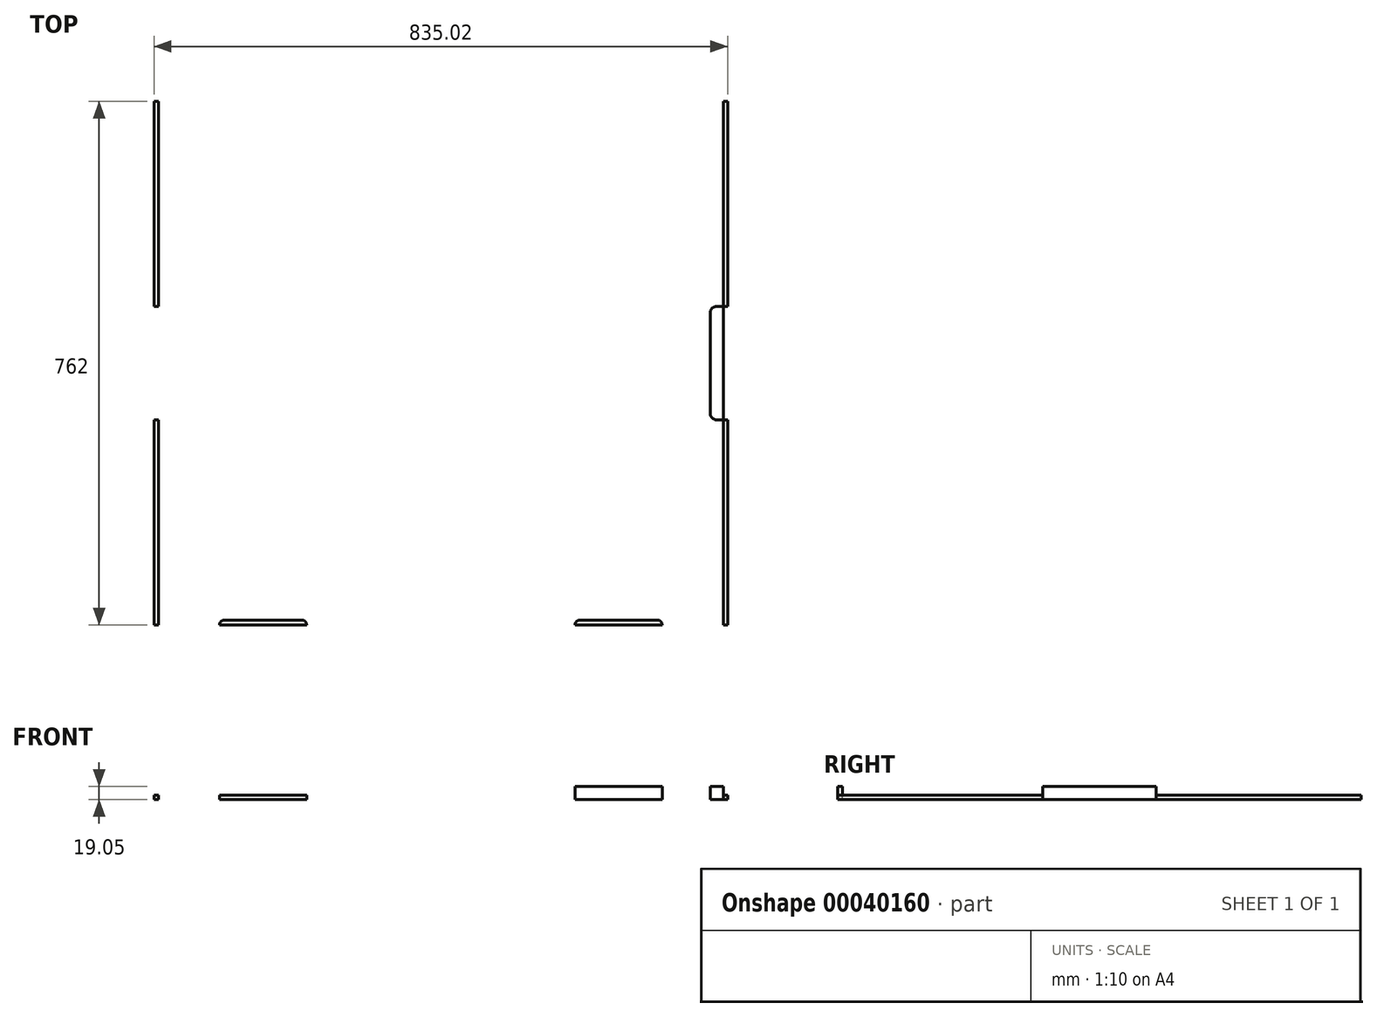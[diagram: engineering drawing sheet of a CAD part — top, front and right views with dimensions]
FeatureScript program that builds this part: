
annotation { "Feature Type Name" : "Feature", "Feature Type Description" : "" }
export const myFeature = defineFeature(function(context is Context, id is Id, definition is map)
    precondition{}
    {
        {
            var Q0;
            Q0=qCreatedBy(makeId("Top.planeOp"),FACE);
            var sketch = newSketch(context, id + "F0", { "sketchPlane" : qUnion([Q0])});
            skLineSegment(sketch, "E0.rect.bottom", {"start": v(417.51, -381) * mm, "end": v(-417.51, -381) * mm});
            skLineSegment(sketch, "E0.rect.top", {"start": v(417.51, 381) * mm, "end": v(-417.51, 381) * mm});
            skLineSegment(sketch, "E0.rect.left", {"start": v(417.51, -381) * mm, "end": v(417.51, 381) * mm});
            skLineSegment(sketch, "E0.rect.right", {"start": v(-417.51, -381) * mm, "end": v(-417.51, 381) * mm});
            skPoint(sketch, "E0.rect.middle", {"position": v(0, 0) * mm});
            skSolve(sketch);
        }
        {
            var Q0;
            Q0=makeQuery(id+"F0.imprint","IMPRINT",FACE,{"disambiguationData":[TD([[makeQuery(id+"F0.imprint","IMPRINT",EDGE,{"derivedFrom":sQuery(id+"F0.wireOp",EDGE,"E0.rect.bottom")}),-1.0]])]});
            extrude(context, id + "F1", {"entities" : qUnion([Q0]), "depth" : 19.05 * mm});
        }
        {
            var Q0;
            Q0=makeQuery(id+"F1.opExtrude","CAP_FACE",FACE,{"disambiguationData":[OSD([sQuery(id+"F0.wireOp",EDGE,"E0.rect.bottom"),sQuery(id+"F0.wireOp",EDGE,"E0.rect.top"),sQuery(id+"F0.wireOp",EDGE,"E0.rect.left"),sQuery(id+"F0.wireOp",EDGE,"E0.rect.right")])],"isStart":false});
            var sketch = newSketch(context, id + "F2", { "sketchPlane" : qUnion([Q0])});
            skLineSegment(sketch, "E1.bottom", {"start": v(-423.86, 82.55) * mm, "end": v(-401.64, 82.55) * mm});
            skLineSegment(sketch, "E1.top", {"start": v(-423.86, -82.55) * mm, "end": v(-401.64, -82.55) * mm});
            skLineSegment(sketch, "E1.left", {"start": v(-423.86, 82.55) * mm, "end": v(-423.86, -82.55) * mm});
            skLineSegment(sketch, "E1.right", {"start": v(-392.11, 73.02) * mm, "end": v(-392.11, -73.03) * mm});
            skLineSegment(sketch, "E2.bottom", {"start": v(-195.26, -386.56) * mm, "end": v(-322.26, -386.56) * mm});
            skLineSegment(sketch, "E2.top", {"start": v(-202.4, -373.86) * mm, "end": v(-315.12, -373.86) * mm});
            skLineSegment(sketch, "E2.left", {"start": v(-195.26, -386.56) * mm, "end": v(-195.26, -381) * mm});
            skLineSegment(sketch, "E2.right", {"start": v(-322.26, -386.56) * mm, "end": v(-322.26, -381) * mm});
            skLineSegment(sketch, "E3.bottom", {"start": v(-461.96, 387.35) * mm, "end": v(-411.16, 387.35) * mm});
            skLineSegment(sketch, "E3.top", {"start": v(-461.96, -387.35) * mm, "end": v(-411.16, -387.35) * mm});
            skLineSegment(sketch, "E3.left", {"start": v(-461.96, 387.35) * mm, "end": v(-461.96, -387.35) * mm});
            skLineSegment(sketch, "E3.right", {"start": v(-411.16, 387.35) * mm, "end": v(-411.16, -387.35) * mm});
            skPoint(sketch, "E4.visualSharp", {"position": v(-392.11, 82.55) * mm});
            skArc(sketch, "E4.filletArc", {"start": v(-392.11, 73.02) * mm, "mid": v(-394.9, 79.76) * mm, "end": v(-401.64, 82.55) * mm});
            skPoint(sketch, "E5.visualSharp", {"position": v(-392.11, -82.55) * mm});
            skArc(sketch, "E5.filletArc", {"start": v(-401.64, -82.55) * mm, "mid": v(-394.9, -79.76) * mm, "end": v(-392.11, -73.03) * mm});
            skLineSegment(sketch, "E6", {"start": v(0, 0) * mm, "end": v(0, 252.74) * mm, "construction": true});
            skArc(sketch, "E7.MirrorCS", {"start": v(392.11, 73.02) * mm, "mid": v(394.9, 79.76) * mm, "end": v(401.64, 82.55) * mm});
            skArc(sketch, "E8.MirrorCS", {"start": v(401.64, -82.55) * mm, "mid": v(394.9, -79.76) * mm, "end": v(392.11, -73.03) * mm});
            skLineSegment(sketch, "E9.MirrorCS", {"start": v(392.11, 73.02) * mm, "end": v(392.11, -73.03) * mm});
            skLineSegment(sketch, "E10.MirrorCS", {"start": v(461.96, 387.35) * mm, "end": v(411.16, 387.35) * mm});
            skLineSegment(sketch, "E11.MirrorCS", {"start": v(461.96, -387.35) * mm, "end": v(411.16, -387.35) * mm});
            skLineSegment(sketch, "E12.MirrorCS", {"start": v(461.96, 387.35) * mm, "end": v(461.96, -387.35) * mm});
            skLineSegment(sketch, "E13.MirrorCS", {"start": v(411.16, 387.35) * mm, "end": v(411.16, -387.35) * mm});
            skLineSegment(sketch, "E14.MirrorCS", {"start": v(423.86, 82.55) * mm, "end": v(423.86, -82.55) * mm});
            skLineSegment(sketch, "E15.MirrorCS", {"start": v(423.86, -82.55) * mm, "end": v(401.64, -82.55) * mm});
            skLineSegment(sketch, "E16.MirrorCS", {"start": v(423.86, 82.55) * mm, "end": v(401.64, 82.55) * mm});
            skPoint(sketch, "E17.MirrorP", {"position": v(392.11, -82.55) * mm});
            skPoint(sketch, "E18.MirrorP", {"position": v(392.11, 82.55) * mm});
            skPoint(sketch, "E19.visualSharp", {"position": v(-322.26, -373.86) * mm});
            skArc(sketch, "E19.filletArc", {"start": v(-315.12, -373.86) * mm, "mid": v(-320.17, -375.95) * mm, "end": v(-322.26, -381) * mm});
            skPoint(sketch, "E20.visualSharp", {"position": v(-195.26, -373.86) * mm});
            skArc(sketch, "E20.filletArc", {"start": v(-195.26, -381) * mm, "mid": v(-197.35, -375.95) * mm, "end": v(-202.4, -373.86) * mm});
            skLineSegment(sketch, "E21.MirrorCS", {"start": v(195.26, -386.56) * mm, "end": v(195.26, -381) * mm});
            skLineSegment(sketch, "E22.MirrorCS", {"start": v(322.26, -386.56) * mm, "end": v(322.26, -381) * mm});
            skArc(sketch, "E23.MirrorCS", {"start": v(195.26, -381) * mm, "mid": v(197.35, -375.95) * mm, "end": v(202.4, -373.86) * mm});
            skArc(sketch, "E24.MirrorCS", {"start": v(315.12, -373.86) * mm, "mid": v(320.17, -375.95) * mm, "end": v(322.26, -381) * mm});
            skPoint(sketch, "E25.MirrorP", {"position": v(322.26, -373.86) * mm});
            skPoint(sketch, "E26.MirrorP", {"position": v(195.26, -373.86) * mm});
            skLineSegment(sketch, "E27.MirrorCS", {"start": v(202.4, -373.86) * mm, "end": v(315.12, -373.86) * mm});
            skLineSegment(sketch, "E28.MirrorCS", {"start": v(195.26, -386.56) * mm, "end": v(322.26, -386.56) * mm});
            skSolve(sketch);
        }
        {
            var Q0;
            {var subQ5=sQuery(id+"F2.wireOp",EDGE,"E1.left");Q0=makeQuery(id+"F2.imprint","IMPRINT",FACE,{"disambiguationData":[TD([[makeQuery(id+"F2.imprint","IMPRINT",EDGE,{"derivedFrom":subQ5}),1.0]])]});}
            var Q1;
            {var subQ3=sQuery(id+"F2.wireOp",EDGE,"E1.bottom");var subQ5=sQuery(id+"F2.wireOp",EDGE,"E3.right");var subQ7=makeQuery(id+"F2.imprint","INTERSECT",VERTEX,{"derivedFrom":[subQ3,subQ5]});Q1=makeQuery(id+"F2.imprint","IMPRINT",FACE,{"disambiguationData":[TD([[makeQuery(id+"F2.imprint","IMPRINT",EDGE,{"disambiguationData":[TD([[subQ7,1.0]])],"derivedFrom":subQ3}),-1.0]])]});}
            var Q2;
            Q2=makeQuery(id+"F2.imprint","IMPRINT",FACE,{"disambiguationData":[TD([[makeQuery(id+"F2.imprint","IMPRINT",EDGE,{"derivedFrom":sQuery(id+"F2.wireOp",EDGE,"E1.right")}),-1.0]])]});
            var Q3;
            {var subQ0=sQuery(id+"F2.wireOp",EDGE,"E7.MirrorCS");Q3=makeQuery(id+"F2.imprint","IMPRINT",FACE,{"disambiguationData":[TD([[makeQuery(id+"F2.imprint","IMPRINT",EDGE,{"derivedFrom":subQ0}),-1.0]])]});}
            var Q4;
            {var subQ5=sQuery(id+"F2.wireOp",EDGE,"E14.MirrorCS");Q4=makeQuery(id+"F2.imprint","IMPRINT",FACE,{"disambiguationData":[TD([[makeQuery(id+"F2.imprint","IMPRINT",EDGE,{"derivedFrom":subQ5}),-1.0]])]});}
            var Q5;
            {var subQ0=sQuery(id+"F2.wireOp",EDGE,"E16.MirrorCS");var subQ3=sQuery(id+"F2.wireOp",EDGE,"E13.MirrorCS");var subQ4=makeQuery(id+"F2.imprint","INTERSECT",VERTEX,{"derivedFrom":[subQ3,subQ0]});Q5=makeQuery(id+"F2.imprint","IMPRINT",FACE,{"disambiguationData":[TD([[makeQuery(id+"F2.imprint","IMPRINT",EDGE,{"disambiguationData":[TD([[subQ4,-1.0]])],"derivedFrom":subQ3}),1.0]])]});}
            extrude(context, id + "F3", {"entities" : qUnion([Q0, Q1, Q2, Q3, Q4, Q5]), "operationType" : NewBodyOperationType.REMOVE, "endBound" : BoundingType.THROUGH_ALL, "oppositeDirection" : true, "depth" : 25.4 * mm});
        }
        {
            var Q0;
            {var subQ1=sQuery(id+"F2.wireOp",EDGE,"E1.bottom");var subQ5=sQuery(id+"F2.wireOp",EDGE,"E3.right");var subQ7=makeQuery(id+"F2.imprint","INTERSECT",VERTEX,{"derivedFrom":[subQ1,subQ5]});Q0=makeQuery(id+"F2.imprint","IMPRINT",FACE,{"disambiguationData":[TD([[makeQuery(id+"F2.imprint","IMPRINT",EDGE,{"disambiguationData":[TD([[subQ7,1.0]])],"derivedFrom":subQ1}),1.0]])]});}
            var Q1;
            {var subQ1=sQuery(id+"F2.wireOp",EDGE,"E1.top");var subQ5=sQuery(id+"F2.wireOp",EDGE,"E3.right");var subQ7=makeQuery(id+"F2.imprint","INTERSECT",VERTEX,{"derivedFrom":[subQ1,subQ5]});Q1=makeQuery(id+"F2.imprint","IMPRINT",FACE,{"disambiguationData":[TD([[makeQuery(id+"F2.imprint","IMPRINT",EDGE,{"disambiguationData":[TD([[subQ7,1.0]])],"derivedFrom":subQ1}),-1.0]])]});}
            var Q2;
            {var subQ1=sQuery(id+"F2.wireOp",EDGE,"E13.MirrorCS");var subQ5=sQuery(id+"F2.wireOp",EDGE,"E16.MirrorCS");var subQ7=makeQuery(id+"F2.imprint","INTERSECT",VERTEX,{"derivedFrom":[subQ1,subQ5]});Q2=makeQuery(id+"F2.imprint","IMPRINT",FACE,{"disambiguationData":[TD([[makeQuery(id+"F2.imprint","IMPRINT",EDGE,{"disambiguationData":[TD([[subQ7,1.0]])],"derivedFrom":subQ1}),1.0]])]});}
            var Q3;
            {var subQ1=sQuery(id+"F2.wireOp",EDGE,"E13.MirrorCS");var subQ5=sQuery(id+"F2.wireOp",EDGE,"E15.MirrorCS");var subQ7=makeQuery(id+"F2.imprint","INTERSECT",VERTEX,{"derivedFrom":[subQ1,subQ5]});Q3=makeQuery(id+"F2.imprint","IMPRINT",FACE,{"disambiguationData":[TD([[makeQuery(id+"F2.imprint","IMPRINT",EDGE,{"disambiguationData":[TD([[subQ7,-1.0]])],"derivedFrom":subQ1}),1.0]])]});}
            var Q4;
            {var subQ2=sQuery(id+"F2.wireOp",EDGE,"E23.MirrorCS");Q4=makeQuery(id+"F2.imprint","IMPRINT",FACE,{"disambiguationData":[TD([[makeQuery(id+"F2.imprint","IMPRINT",EDGE,{"derivedFrom":subQ2}),-1.0]])]});}
            var Q5;
            Q5=makeQuery(id+"F2.imprint","IMPRINT",FACE,{"disambiguationData":[TD([[makeQuery(id+"F2.imprint","IMPRINT",EDGE,{"derivedFrom":sQuery(id+"F2.wireOp",EDGE,"E2.top")}),1.0]])]});
            extrude(context, id + "F4", {"entities" : qUnion([Q0, Q1, Q2, Q3, Q4, Q5]), "operationType" : NewBodyOperationType.REMOVE, "oppositeDirection" : true, "depth" : 12.7 * mm});
        }
        {
            var Q0;
            Q0=makeQuery(id+"F1.opExtrude","CAP_FACE",FACE,{"disambiguationData":[OSD([sQuery(id+"F0.wireOp",EDGE,"E0.rect.bottom"),sQuery(id+"F0.wireOp",EDGE,"E0.rect.top"),sQuery(id+"F0.wireOp",EDGE,"E0.rect.left"),sQuery(id+"F0.wireOp",EDGE,"E0.rect.right")])],"isStart":false});
            var sketch = newSketch(context, id + "F5", { "sketchPlane" : qUnion([Q0])});
            skCircle(sketch, "E29", {"center": v(-368.3, 63.5) * mm, "radius": 4.01 * mm});
            skLineSegment(sketch, "E30", {"start": v(0, 0) * mm, "end": v(0, 204.5) * mm, "construction": true});
            skLineSegment(sketch, "E31", {"start": v(0, 0) * mm, "end": v(-237.68, 0) * mm, "construction": true});
            skCircle(sketch, "E32.0.1.0", {"center": v(-368.3, 88.9) * mm, "radius": 4.01 * mm});
            skCircle(sketch, "E32.0.2.0", {"center": v(-368.3, 114.3) * mm, "radius": 4.01 * mm});
            skCircle(sketch, "E32.0.3.0", {"center": v(-368.3, 139.7) * mm, "radius": 4.01 * mm});
            skCircle(sketch, "E32.0.4.0", {"center": v(-368.3, 165.1) * mm, "radius": 4.01 * mm});
            skCircle(sketch, "E32.0.5.0", {"center": v(-368.3, 190.5) * mm, "radius": 4.01 * mm});
            skCircle(sketch, "E32.0.6.0", {"center": v(-368.3, 215.9) * mm, "radius": 4.01 * mm});
            skCircle(sketch, "E32.0.7.0", {"center": v(-368.3, 241.3) * mm, "radius": 4.01 * mm});
            skCircle(sketch, "E32.0.8.0", {"center": v(-368.3, 266.7) * mm, "radius": 4.01 * mm});
            skCircle(sketch, "E32.0.9.0", {"center": v(-368.3, 292.1) * mm, "radius": 4.01 * mm});
            skCircle(sketch, "E32.0.10.0", {"center": v(-368.3, 317.5) * mm, "radius": 4.01 * mm});
            skCircle(sketch, "E32.0.11.0", {"center": v(-368.3, 342.9) * mm, "radius": 4.01 * mm});
            skCircle(sketch, "E32.0.12.0", {"center": v(-368.3, 368.3) * mm, "radius": 4.01 * mm});
            skLineSegment(sketch, "E32.direction1", {"start": v(-368.3, 63.5) * mm, "end": v(-342.9, 63.5) * mm, "construction": true});
            skLineSegment(sketch, "E32.direction2", {"start": v(-368.3, 63.5) * mm, "end": v(-368.3, 88.9) * mm, "construction": true});
            skCircle(sketch, "E33.MirrorC", {"center": v(368.3, 317.5) * mm, "radius": 4.01 * mm});
            skCircle(sketch, "E34.MirrorC", {"center": v(368.3, 292.1) * mm, "radius": 4.01 * mm});
            skCircle(sketch, "E35.MirrorC", {"center": v(368.3, 266.7) * mm, "radius": 4.01 * mm});
            skCircle(sketch, "E36.MirrorC", {"center": v(368.3, 241.3) * mm, "radius": 4.01 * mm});
            skCircle(sketch, "E37.MirrorC", {"center": v(368.3, 215.9) * mm, "radius": 4.01 * mm});
            skCircle(sketch, "E38.MirrorC", {"center": v(368.3, 190.5) * mm, "radius": 4.01 * mm});
            skCircle(sketch, "E39.MirrorC", {"center": v(368.3, 165.1) * mm, "radius": 4.01 * mm});
            skCircle(sketch, "E40.MirrorC", {"center": v(368.3, 139.7) * mm, "radius": 4.01 * mm});
            skCircle(sketch, "E41.MirrorC", {"center": v(368.3, 114.3) * mm, "radius": 4.01 * mm});
            skCircle(sketch, "E42.MirrorC", {"center": v(368.3, 368.3) * mm, "radius": 4.01 * mm});
            skCircle(sketch, "E43.MirrorC", {"center": v(368.3, 342.9) * mm, "radius": 4.01 * mm});
            skCircle(sketch, "E44.MirrorC", {"center": v(368.3, 88.9) * mm, "radius": 4.01 * mm});
            skCircle(sketch, "E45.MirrorC", {"center": v(368.3, 63.5) * mm, "radius": 4.01 * mm});
            skCircle(sketch, "E46.MirrorC", {"center": v(-368.3, -63.5) * mm, "radius": 4.01 * mm});
            skCircle(sketch, "E47.MirrorC", {"center": v(-368.3, -88.9) * mm, "radius": 4.01 * mm});
            skCircle(sketch, "E48.MirrorC", {"center": v(-368.3, -317.5) * mm, "radius": 4.01 * mm});
            skCircle(sketch, "E49.MirrorC", {"center": v(-368.3, -292.1) * mm, "radius": 4.01 * mm});
            skCircle(sketch, "E50.MirrorC", {"center": v(-368.3, -266.7) * mm, "radius": 4.01 * mm});
            skCircle(sketch, "E51.MirrorC", {"center": v(-368.3, -241.3) * mm, "radius": 4.01 * mm});
            skCircle(sketch, "E52.MirrorC", {"center": v(-368.3, -215.9) * mm, "radius": 4.01 * mm});
            skCircle(sketch, "E53.MirrorC", {"center": v(368.3, -292.1) * mm, "radius": 4.01 * mm});
            skCircle(sketch, "E54.MirrorC", {"center": v(-368.3, -190.5) * mm, "radius": 4.01 * mm});
            skCircle(sketch, "E55.MirrorC", {"center": v(-368.3, -165.1) * mm, "radius": 4.01 * mm});
            skCircle(sketch, "E56.MirrorC", {"center": v(-368.3, -139.7) * mm, "radius": 4.01 * mm});
            skCircle(sketch, "E57.MirrorC", {"center": v(368.3, -190.5) * mm, "radius": 4.01 * mm});
            skCircle(sketch, "E58.MirrorC", {"center": v(-368.3, -114.3) * mm, "radius": 4.01 * mm});
            skCircle(sketch, "E59.MirrorC", {"center": v(368.3, -368.3) * mm, "radius": 4.01 * mm});
            skCircle(sketch, "E60.MirrorC", {"center": v(368.3, -266.7) * mm, "radius": 4.01 * mm});
            skCircle(sketch, "E61.MirrorC", {"center": v(368.3, -342.9) * mm, "radius": 4.01 * mm});
            skCircle(sketch, "E62.MirrorC", {"center": v(368.3, -63.5) * mm, "radius": 4.01 * mm});
            skCircle(sketch, "E63.MirrorC", {"center": v(368.3, -241.3) * mm, "radius": 4.01 * mm});
            skCircle(sketch, "E64.MirrorC", {"center": v(368.3, -165.1) * mm, "radius": 4.01 * mm});
            skCircle(sketch, "E65.MirrorC", {"center": v(368.3, -317.5) * mm, "radius": 4.01 * mm});
            skCircle(sketch, "E66.MirrorC", {"center": v(368.3, -88.9) * mm, "radius": 4.01 * mm});
            skCircle(sketch, "E67.MirrorC", {"center": v(368.3, -139.7) * mm, "radius": 4.01 * mm});
            skCircle(sketch, "E68.MirrorC", {"center": v(368.3, -215.9) * mm, "radius": 4.01 * mm});
            skCircle(sketch, "E69.MirrorC", {"center": v(-368.3, -342.9) * mm, "radius": 4.01 * mm});
            skCircle(sketch, "E70.MirrorC", {"center": v(-368.3, -368.3) * mm, "radius": 4.01 * mm});
            skCircle(sketch, "E71.MirrorC", {"center": v(368.3, -114.3) * mm, "radius": 4.01 * mm});
            skLineSegment(sketch, "E72.MirrorCS", {"start": v(-368.3, -63.5) * mm, "end": v(-342.9, -63.5) * mm});
            skLineSegment(sketch, "E73.MirrorCS", {"start": v(-368.3, -63.5) * mm, "end": v(-368.3, -88.9) * mm});
            skCircle(sketch, "E74", {"center": v(-368.3, 0) * mm, "radius": 6.35 * mm});
            skCircle(sketch, "E75.MirrorC", {"center": v(368.3, 0) * mm, "radius": 6.35 * mm});
            skSolve(sketch);
        }
        {
            var Q0;
            Q0 = qSketchRegion(id + "F5", true);
            extrude(context, id + "F6", {"entities" : qUnion([Q0]), "operationType" : NewBodyOperationType.REMOVE, "oppositeDirection" : true, "depth" : 25.4 * mm});
        }
    });
